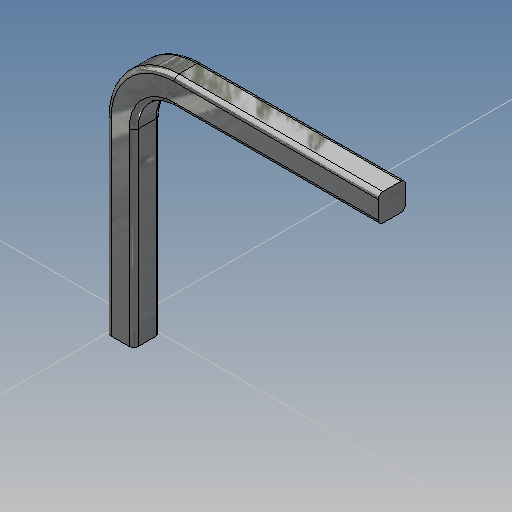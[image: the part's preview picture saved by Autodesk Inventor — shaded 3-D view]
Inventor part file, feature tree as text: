
AUTODESK INVENTOR PART (.ipt)
format: ipt  version: 2019 (Build 230136000, 136)  size: 150,016 bytes
history: native  units: in
note: dims shown in document units (in); Inventor stores cm internally (conversion verified against a paired STEP export)
features: extrude x1, fillet x1, sketch x1
ambient origin geometry x8: Origin, YZ Plane, XZ Plane, XY Plane, X Axis, Y Axis, Z Axis, Center Point
bodies: Solid1 (feature_tree)
feature tree (3):
  extrude  "Extrusion1"  Depth=0.03in
  fillet  "Fillet2"  Radius=0.045in
  sketch  "Sketch1"  dims[d0=0.3in d1=0.03in d2=0.045in d3=0.075in d4=0.095in d5=0.188in d6=0.03in d7=0.0in d9=0.005in]
